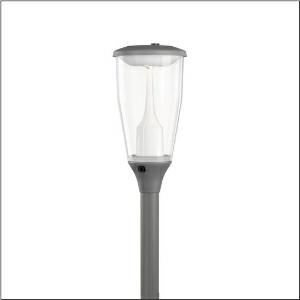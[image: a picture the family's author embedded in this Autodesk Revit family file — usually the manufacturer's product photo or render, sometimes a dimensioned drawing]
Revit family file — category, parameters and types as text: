
# Revit family: dl_11_iq___st1_2a_5xa5575ew14h000022_afae
name_source: partatom
category: Lighting Fixtures
units: mm (PartAtom-declared; Revit-internal decimal feet)

## family parameters
Cut with Voids When Loaded = No
Host = Face
Light Source = No
Part Type = Normal
Room Calculation Point = No
Round Connector Dimension = Use Diameter
Shared = No

## types (1)
- --- (1 x LED, 1560 lm, 10.7 W, 3000K)
    Apparent Load = 11 VA
    CIE Flux Codes = 24 63 94 96 100
    Color Rendering = 70
    Color Temperature = 3000K
    Default Elevation = 1800 mm
    Description = DL 11 iQ, mast luminaire, Module 540 iQ-SR, primary light control with 3 zone facetted reflector, of plastic, silver coated, highly specular, structured, primary optical cover: cover, of PMMA, transparent, light distribution: ST1.2a, light emission: direct distribution, primary light characteristic: asymmetric, installation type: post-top, LED, High Power LED, rated luminous flux: 1.560lm, luminous efficacy: 146lm/W, light colour: 730, colour temperature: 3000K, control gear: iQ-Street Remote, D4i with power reduction, control: pre-setting: logarithmic dimming characteristic, Street-Remote, Auto-Match, Temp-Guard, Lumen-Switch, Night-Set, Smart-Wire, Light-Fading, Desk-Remote (wireless, voltage-free reading and setting of iQ features in the workshop via application-optimized NFC function/RFID function), optimised constant luminous flux control (CLO 2.0), mains connection: 220..240V, AC, 50/60Hz, connection cable pre-assembled, cable length: 5,5m, start of lifetime: 11W, end of service life: 11W, reduction: 6W, luminaire housing, upper part, of diecast aluminium, coated, SITECO metallic grey (DB 702S), spigot size: 76mm (post-top), mounting height: 3..5m, post-top mast mounting element, of diecast aluminium, coated, SITECO metallic grey (DB 702S), Module 540 iQ-SR, traffic white (RAL 9016), equipment: standard, Smart Interface above and design motion detector below, protection rating (complete): IP65, insulation class (complete): insulation class II (safety insulation), certification: CE, ENEC, ENEC+, VDE, impact resistance: IK07, packaging unit: 1 piece

Light Distribution: ST1.2a
    Height = 665 mm
    Lamp = 1 x LED
    Lamp Light Flux = 1560 lm
    Lamp Power = 10.7 W
    Lamp count = 1
    Length = 334 mm
    Luminous efficacy = 146 lm/W
    Manufacturer = Siteco
    ModVariant = No
    Model = 5XA5575EW14H000022
    Number of Poles = 1
    OnlyDefault = Yes
    Power Factor = 1
    Product Name = DL 11 iQ | ST1.2a
    Product group = mast luminaire | pylon top
    ProductGroupID = 6100
    Protection Class = Protection class II
    Protection Degree = IP 65
    RLX_Detail_Level = 1
    RLX_Emergency_Light_Flux = 0 lm
    RLX_Emergency_Type = 0
    RLX_Emergency_Type_DB = No
    RlxData = <blob elided: 158665 chars, md5=27d97767>
    Socket = socket
    Standby Power = 0 W
    System Light Flux = 1560 lm
    System Power = 11 W
    Type Comments = factory setting: luminous flux: 100 % | dim-lin: 254 | 419 mA
    Type Image = l_1337543.jpg
    URL = http://relux.com
    VarID = @adj_098615
    Voltage = 0 V
    Weight = 0.00 kg
    Width = 0 mm  [stored 0 ft]

note: [stored X ft] marks values corroborated as IEEE doubles in the binary element streams (Revit-internal decimal feet)

## geometry (parser evidence)
native form markers: Blend x4, Sweep x11
no freeform markers — native parametric forms only
